# Revit family: Поли-Групп_ЗадвижкаКлиноваяEAZ-МК-F4(ВS)_DN700-1600
name_source: partatom
category: Арматура трубопроводов
units: mm (PartAtom-declared; Revit-internal decimal feet)

## family parameters
Всегда вертикально = Да
На основе рабочей плоскости = Нет
Общий = Нет
При загрузке вырезать с полостями = Нет
Размер круглого соединителя = Использовать диаметр
Тип детали = Клапан - Вставляется

## types (7) — shared parameters
ADSK_URL страницы изделия = https://www.polycorr.ru
ADSK_Версия Revit = 2019
ADSK_Единица измерения = шт
ADSK_Завод-изготовитель = ООО ПК «Поли-Групп»
ADSK_Количество = 1
ADSK_Материал = Высокопрочный чугун GGG-40
ADSK_Материал наименование = Высокопрочный чугун с шаровидным графитом (GGG-40)
Kv = 1.0 м³/ч
PN = 10.0 бары
f = 5 мм
Класс герметичности = А по ГОСТ Р 9544-2015
Материал Диска = Высокопрочный чугун с шаровидным графитом (GGG-40)
Материал уплотнителя = PTFE
Назначение = Для установки в качестве запорного устройства на трубопроводах
Покрытие = Высококачественное эпоксидное покрытие толщиной 300 мкм
Рабочая среда = Техническая вода, канализационные стоки, морская вода
Разработчик = https://3dbim.pro
Срок службы = 50 лет
ТВ = Поли-Групп_ЗадвижкаКлиноваяEAZ-МК-F4(ВS)_DN700-1600
Температура рабочей среды = 0 до +70°С
Тип привода = Редуктор
Тип присоединения = Фланцевое

## per-type parameters (varying)
- 10-700: A=1136 мм; ADSK_Марка=EAZ-GV-2-F4 DN700 PN10; ADSK_Масса=1394; ADSK_Масса_Текст=1394; ADSK_Наименование=Задвижка клиновая с металлическим уплотнением EAZ MK F4 для сточных вод фланцевая DN700 PN10; ADSK_Наименование краткое=Задвижка клиновая EAZ MK F4 DN700 PN10; D=895 мм; D1=840 мм; D2=794 мм; DN=700 мм; D_Наружный=709 мм; H1=480 мм; H2=1875 мм; L=430 мм; L1=480 мм; L2=144 мм; R=31 мм; R1=307 мм; b=33 мм; d1=175 мм; h2=1313 мм; l1=258 мм; l2=280 мм; l3=387 мм; t=131 мм; Габаритные размеры=895х430х2355; Корпус_Глубина=909 мм; с=33 мм
- 10-800: A=1223 мм; ADSK_Марка=EAZ-GV-2-F4 DN800 PN10; ADSK_Масса=1780; ADSK_Масса_Текст=1780; ADSK_Наименование=Задвижка клиновая с металлическим уплотнением EAZ MK F4 для сточных вод фланцевая DN800 PN10; ADSK_Наименование краткое=Задвижка клиновая EAZ MK F4 DN800 PN10; D=1015 мм; D1=950 мм; D2=901 мм; DN=800 мм; D_Наружный=809 мм; H1=540 мм; H2=2037 мм; L=470 мм; L1=540 мм; L2=162 мм; R=33 мм; R1=330 мм; b=35 мм; d1=200 мм; h2=1426 мм; l1=282 мм; l2=306 мм; l3=423 мм; t=143 мм; Габаритные размеры=1015х470х2577; Корпус_Глубина=978 мм; с=33 мм
- 10-900: A=1396 мм; ADSK_Марка=EAZ-GV-2-F4 DN900 PN10; ADSK_Масса=2510; ADSK_Масса_Текст=2510; ADSK_Наименование=Задвижка клиновая с металлическим уплотнением EAZ MK F4 для сточных вод фланцевая DN900 PN10; ADSK_Наименование краткое=Задвижка клиновая EAZ MK F4 DN900 PN10; D=1115 мм; D1=1050 мм; D2=1001 мм; DN=900 мм; D_Наружный=909 мм; H1=645 мм; H2=2201 мм; L=510 мм; L1=600 мм; L2=180 мм; R=37 мм; R1=370 мм; b=38 мм; d1=225 мм; h2=1541 мм; l1=306 мм; l2=332 мм; l3=459 мм; t=154 мм; Габаритные размеры=1115х510х2846; Корпус_Глубина=1117 мм; с=88 мм
- 10-1000: A=1468 мм; ADSK_Марка=EAZ-GV-2-F4 DN1000 PN10; ADSK_Масса=3175; ADSK_Масса_Текст=3175; ADSK_Наименование=Задвижка клиновая с металлическим уплотнением EAZ MK F4 для сточных вод фланцевая DN1000 PN10; ADSK_Наименование краткое=Задвижка клиновая EAZ MK F4 DN1000 PN10; D=1230 мм; D1=1160 мм; D2=1112 мм; DN=1000 мм; D_Наружный=1009 мм; H1=680 мм; H2=2480 мм; L=550 мм; L1=700 мм; L2=210 мм; R=39 мм; R1=390 мм; b=40 мм; d1=250 мм; h2=1736 мм; l1=330 мм; l2=358 мм; l3=495 мм; t=174 мм; Габаритные размеры=1230х550х3160; Корпус_Глубина=1174 мм; с=65 мм
- 10-1200: A=1625 мм; ADSK_Марка=EAZ-GV-2-F4 DN1200 PN10; ADSK_Масса=4380; ADSK_Масса_Текст=4380; ADSK_Наименование=Задвижка клиновая с металлическим уплотнением EAZ MK F4 для сточных вод фланцевая DN1200 PN10; ADSK_Наименование краткое=Задвижка клиновая EAZ MK F4 DN1200 PN10; D=1455 мм; D1=1380 мм; D2=1328 мм; DN=1200 мм; D_Наружный=1209 мм; H1=800 мм; H2=2786 мм; L=630 мм; L1=800 мм; L2=240 мм; R=43 мм; R1=430 мм; b=45 мм; d1=300 мм; h2=1950 мм; l1=378 мм; l2=410 мм; l3=567 мм; t=195 мм; Габаритные размеры=1455х630х3586; Корпус_Глубина=1300 мм; с=73 мм
- 10-1400: A=1860 мм; ADSK_Марка=EAZ-GV-2-F4 DN1400 PN10; ADSK_Масса=6870; ADSK_Масса_Текст=6870; ADSK_Наименование=Задвижка клиновая с металлическим уплотнением EAZ MK F4 для сточных вод фланцевая DN1400 PN10; ADSK_Наименование краткое=Задвижка клиновая EAZ MK F4 DN1400 PN10; D=1675 мм; D1=1590 мм; D2=1530 мм; DN=1400 мм; D_Наружный=1409 мм; H1=870 мм; H2=3046 мм; L=710 мм; L1=870 мм; L2=261 мм; R=51 мм; R1=510 мм; b=46 мм; d1=350 мм; h2=2132 мм; l1=426 мм; l2=462 мм; l3=639 мм; t=213 мм; Габаритные размеры=1675х710х3916; Корпус_Глубина=1488 мм; с=33 мм
- 10-1600: A=2065 мм; ADSK_Марка=EAZ-GV-2-F4 DN1600 PN10; ADSK_Масса=8950; ADSK_Масса_Текст=8950; ADSK_Наименование=Задвижка клиновая с металлическим уплотнением EAZ MK F4 для сточных вод фланцевая DN1600 PN10; ADSK_Наименование краткое=Задвижка клиновая EAZ MK F4 DN1600 PN10; D=1915 мм; D1=1820 мм; D2=1750 мм; DN=1600 мм; D_Наружный=1609 мм; H1=1000 мм; H2=3459 мм; L=790 мм; L1=1000 мм; L2=300 мм; R=63 мм; R1=630 мм; b=49 мм; d1=400 мм; h2=2421 мм; l1=474 мм; l2=514 мм; l3=711 мм; t=242 мм; Габаритные размеры=1915х790х4459; Корпус_Глубина=1652 мм; с=43 мм
